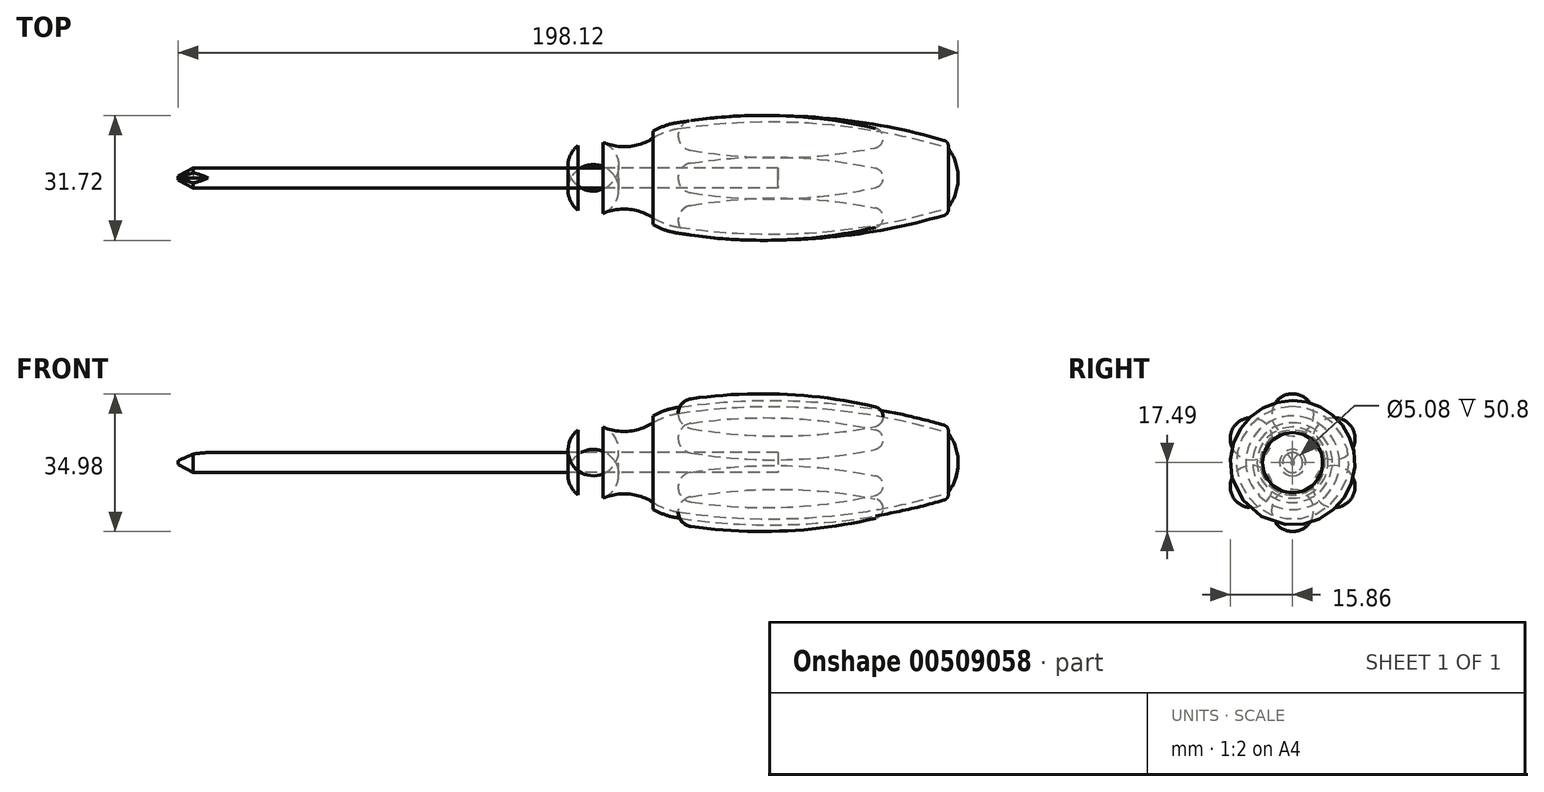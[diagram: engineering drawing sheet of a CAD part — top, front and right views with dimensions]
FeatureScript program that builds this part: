
annotation { "Feature Type Name" : "Feature", "Feature Type Description" : "" }
export const myFeature = defineFeature(function(context is Context, id is Id, definition is map)
    precondition{}
    {
        {
            var Q0;
            Q0=qCreatedBy(makeId("Front.planeOp"),FACE);
            var sketch = newSketch(context, id + "F0", { "sketchPlane" : qUnion([Q0])});
            skLineSegment(sketch, "E0", {"start": v(-101.6, 0) * mm, "end": v(96.52, 0) * mm});
            skLineSegment(sketch, "E1", {"start": v(96.52, 0) * mm, "end": v(117.55, 0) * mm, "construction": true});
            skLineSegment(sketch, "E2", {"start": v(50.8, 2.54) * mm, "end": v(-97.8, 2.54) * mm});
            skLineSegment(sketch, "E3", {"start": v(-101.6, 0.5) * mm, "end": v(-101.6, 0) * mm});
            skLineSegment(sketch, "E4", {"start": v(0, 2.54) * mm, "end": v(0, 8.25) * mm});
            skArc(sketch, "E5", {"start": v(6.35, 9.02) * mm, "mid": v(3.07, 9.48) * mm, "end": v(0, 8.25) * mm});
            skArc(sketch, "E6", {"start": v(6.35, 9.02) * mm, "mid": v(12.84, 7.99) * mm, "end": v(19.05, 10.11) * mm});
            skArc(sketch, "E7", {"start": v(25.4, 12.52) * mm, "mid": v(22.1, 11.65) * mm, "end": v(19.05, 10.11) * mm});
            skArc(sketch, "E8", {"start": v(93.98, 7.62) * mm, "mid": v(59.96, 13.9) * mm, "end": v(25.4, 12.52) * mm});
            skArc(sketch, "E9", {"start": v(96.52, 0) * mm, "mid": v(95.87, 4.02) * mm, "end": v(93.98, 7.62) * mm});
            skArc(sketch, "E10.0", {"start": v(25.17, 14.02) * mm, "mid": v(22.01, 13.24) * mm, "end": v(19.05, 11.9) * mm});
            skArc(sketch, "E10.1", {"start": v(92.95, 9.52) * mm, "mid": v(59.3, 15.46) * mm, "end": v(25.17, 14.02) * mm});
            skLineSegment(sketch, "E11", {"start": v(19.05, 11.9) * mm, "end": v(19.05, 10.11) * mm});
            skArc(sketch, "E12", {"start": v(93.98, 7.62) * mm, "mid": v(93.86, 8.78) * mm, "end": v(92.95, 9.52) * mm});
            skPoint(sketch, "E13.orphan", {"position": v(0, 0) * mm});
            skLineSegment(sketch, "E14", {"start": v(50.8, 2.54) * mm, "end": v(50.8, 0) * mm});
            skLineSegment(sketch, "E15", {"start": v(-101.6, 0.5) * mm, "end": v(-97.8, 2.54) * mm});
            skPoint(sketch, "E16.orphan", {"position": v(-101.6, 2.54) * mm});
            skSolve(sketch);
        }
        {
            var Q0;
            Q0=qCreatedBy(makeId("Front.planeOp"),FACE);
            var sketch = newSketch(context, id + "F1", { "sketchPlane" : qUnion([Q0])});
            skLineSegment(sketch, "E17", {"start": v(25.4, 12.52) * mm, "end": v(77.47, 11.64) * mm});
            skArc(sketch, "E18", {"start": v(28.67, 16.22) * mm, "mid": v(26.35, 14.97) * mm, "end": v(25.4, 12.52) * mm});
            skArc(sketch, "E19", {"start": v(77.47, 11.64) * mm, "mid": v(76.93, 13.25) * mm, "end": v(75.5, 14.16) * mm});
            skArc(sketch, "E20", {"start": v(75.5, 14.16) * mm, "mid": v(52.19, 17.37) * mm, "end": v(28.67, 16.22) * mm});
            skSolve(sketch);
        }
        {
            var Q0;
            Q0=qCreatedBy(makeId("Front.planeOp"),FACE);
            var sketch = newSketch(context, id + "F2", { "sketchPlane" : qUnion([Q0])});
            skLineSegment(sketch, "E21", {"start": v(-101.6, 0.5) * mm, "end": v(-93.98, 2.54) * mm});
            skSolve(sketch);
        }
        {
            var Q0;
            Q0=sQuery(id+"F2.wireOp",VERTEX,"E21.start");
            var Q1;
            Q1=sQuery(id+"F2.wireOp",EDGE,"E21");
            cPlane(context, id + "F3", {"entities" : qUnion([Q0, Q1]), "cplaneType" : CPlaneType.LINE_POINT, "offset" : 25.4 * mm, "width" : 152.4 * mm, "height" : 152.4 * mm});
        }
        {
            var Q0;
            Q0=qCreatedBy(id+"F3.planeOp",FACE);
            var sketch = newSketch(context, id + "F4", { "sketchPlane" : qUnion([Q0])});
            skLineSegment(sketch, "E22", {"start": v(5.08, 29.2) * mm, "end": v(0, 26.67) * mm});
            skLineSegment(sketch, "E23", {"start": v(0, 26.67) * mm, "end": v(-5.08, 29.2) * mm});
            skLineSegment(sketch, "E24", {"start": v(-5.08, 29.2) * mm, "end": v(5.08, 29.2) * mm});
            skLineSegment(sketch, "E25", {"start": v(0, 29.2) * mm, "end": v(0, 26.67) * mm, "construction": true});
            skSolve(sketch);
        }
        {
            var Q0;
            {var subQ0=sQuery(id+"F0.wireOp",EDGE,"E3");Q0=makeQuery(id+"F0.imprint","IMPRINT",FACE,{"disambiguationData":[TD([[makeQuery(id+"F0.imprint","IMPRINT",EDGE,{"derivedFrom":subQ0}),1.0]])]});}
            var Q1;
            Q1=sQuery(id+"F0.wireOp",EDGE,"E1");
            revolve(context, id + "F5", {"entities" : qUnion([Q0]), "axis" : qUnion([Q1]), "revolveType" : RevolveType.FULL});
        }
        {
            var Q0;
            {var subQ0=sQuery(id+"F0.wireOp",EDGE,"E4");Q0=makeQuery(id+"F0.imprint","IMPRINT",FACE,{"disambiguationData":[TD([[makeQuery(id+"F0.imprint","IMPRINT",EDGE,{"derivedFrom":subQ0}),-1.0]])]});}
            var Q1;
            Q1=sQuery(id+"F0.wireOp",EDGE,"E1");
            revolve(context, id + "F6", {"entities" : qUnion([Q0]), "axis" : qUnion([Q1]), "revolveType" : RevolveType.FULL});
        }
        {
            var Q0;
            Q0=makeQuery(id+"F0.imprint","IMPRINT",FACE,{"disambiguationData":[TD([[makeQuery(id+"F0.imprint","IMPRINT",EDGE,{"derivedFrom":sQuery(id+"F0.wireOp",EDGE,"E7")}),-1.0]])]});
            var Q1;
            Q1=sQuery(id+"F0.wireOp",EDGE,"E1");
            revolve(context, id + "F7", {"entities" : qUnion([Q0]), "axis" : qUnion([Q1]), "revolveType" : RevolveType.FULL});
        }
        {
            var Q0;
            Q0=makeQuery(id+"F1.imprint","IMPRINT",FACE,{"disambiguationData":[TD([[makeQuery(id+"F1.imprint","IMPRINT",EDGE,{"derivedFrom":sQuery(id+"F1.wireOp",EDGE,"E17")}),1.0]])]});
            var Q1;
            Q1=sQuery(id+"F1.wireOp",EDGE,"E17");
            revolve(context, id + "F8", {"entities" : qUnion([Q0]), "axis" : qUnion([Q1]), "revolveType" : RevolveType.FULL});
        }
        {
            var Q0;
            Q0=makeQuery(id+"F8.opRevolve","SWEPT_BODY",BODY,{"disambiguationData":[OSD([sQuery(id+"F1.wireOp",EDGE,"E17"),sQuery(id+"F1.wireOp",EDGE,"E18"),sQuery(id+"F1.wireOp",EDGE,"E19"),sQuery(id+"F1.wireOp",EDGE,"E20")])]});
            var Q1;
            Q1=sQuery(id+"F0.wireOp",EDGE,"E1");
            circularPattern(context, id + "F9", {"entities" : qUnion([Q0]), "axis" : qUnion([Q1]), "angle" : 360 * degree, "instanceCount" : 6, "equalSpace" : true, "computeTransformsWithoutBuiltin" : true});
        }
        {
            var Q0;
            Q0=makeQuery(id+"F6.opRevolve","SWEPT_BODY",BODY,{"disambiguationData":[OSD([sQuery(id+"F0.wireOp",EDGE,"E0"),sQuery(id+"F0.wireOp",EDGE,"E2"),sQuery(id+"F0.wireOp",EDGE,"E4"),sQuery(id+"F0.wireOp",EDGE,"E5"),sQuery(id+"F0.wireOp",EDGE,"E6"),sQuery(id+"F0.wireOp",EDGE,"E7"),sQuery(id+"F0.wireOp",EDGE,"E8"),sQuery(id+"F0.wireOp",EDGE,"E9"),sQuery(id+"F0.wireOp",EDGE,"E14")])]});
            var Q1;
            Q1=makeQuery(id+"F7.opRevolve","SWEPT_BODY",BODY,{"disambiguationData":[OSD([sQuery(id+"F0.wireOp",EDGE,"E7"),sQuery(id+"F0.wireOp",EDGE,"E8"),sQuery(id+"F0.wireOp",EDGE,"E10.0"),sQuery(id+"F0.wireOp",EDGE,"E10.1"),sQuery(id+"F0.wireOp",EDGE,"E11"),sQuery(id+"F0.wireOp",EDGE,"E12")])]});
            booleanBodies(context, id + "F10", {"operationType" : BooleanOperationType.SUBTRACTION, "tools" : qUnion([Q0]), "targets" : qUnion([Q1]), "keepTools" : true});
        }
        {
            var Q0;
            Q0=qSketchRegion(id+"F4",true);
            var Q1;
            Q1=qConstructionFilter(qBodyType(qCreatedBy(id+"F2",EDGE),BodyType.WIRE),ConstructionObject.NO);
            sweep(context, id + "F11", {"operationType" : NewBodyOperationType.REMOVE, "profiles" : qUnion([Q0]), "path" : qUnion([Q1])});
        }
    });
